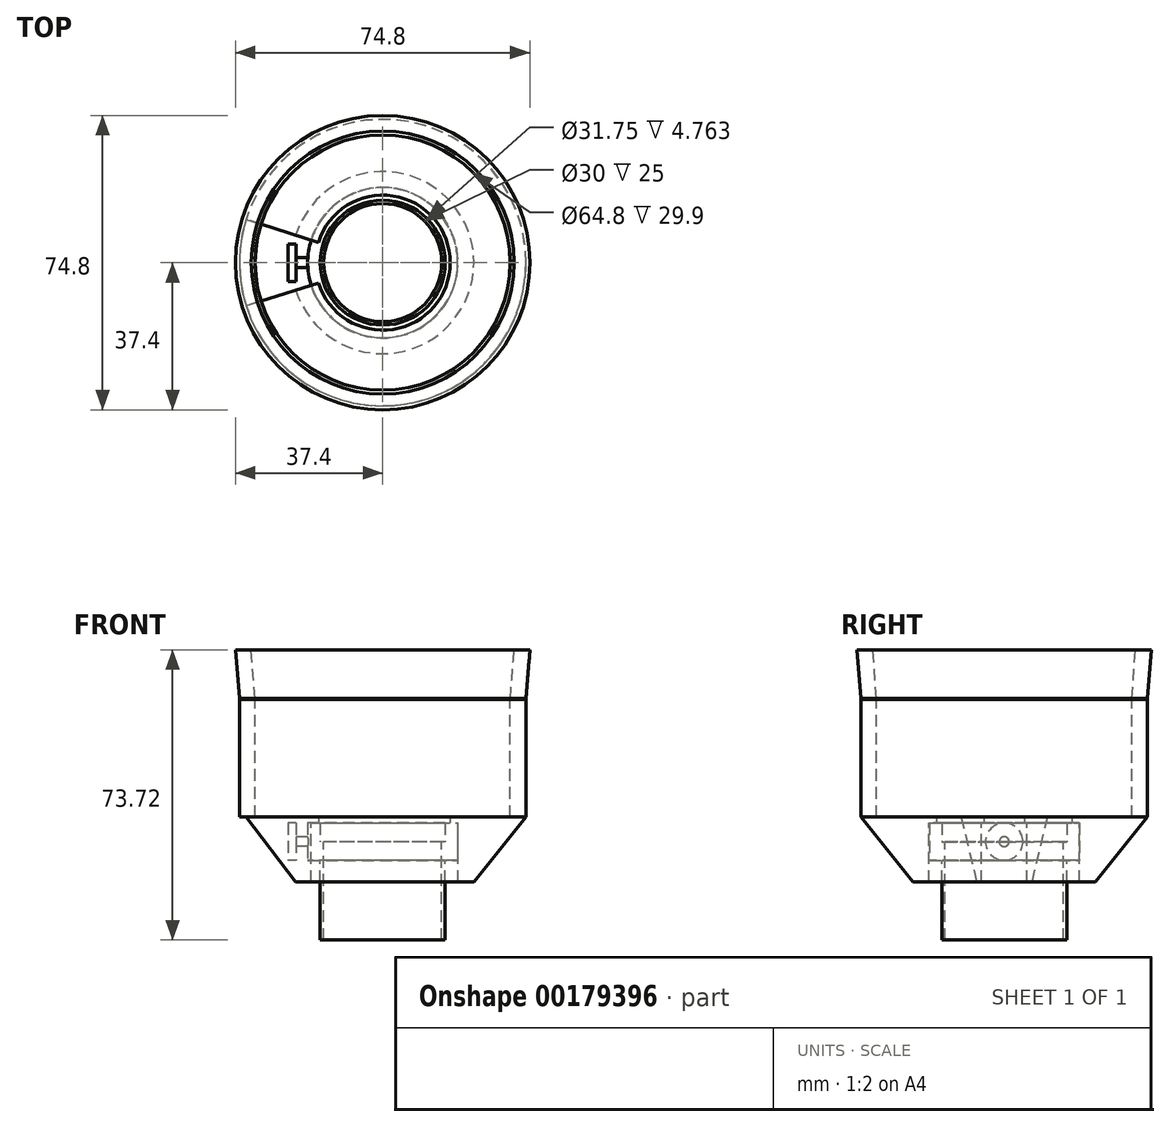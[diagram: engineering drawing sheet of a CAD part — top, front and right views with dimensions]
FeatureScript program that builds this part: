
annotation { "Feature Type Name" : "Feature", "Feature Type Description" : "" }
export const myFeature = defineFeature(function(context is Context, id is Id, definition is map)
    precondition{}
    {
        {
            var Q0;
            Q0=qCreatedBy(makeId("Top.planeOp"),FACE);
            var sketch = newSketch(context, id + "F0", { "sketchPlane" : qUnion([Q0])});
            skCircle(sketch, "E0", {"center": v(0, 0) * mm, "radius": 15.88 * mm});
            skCircle(sketch, "E1", {"center": v(0, 0) * mm, "radius": 19.05 * mm});
            skCircle(sketch, "E2", {"center": v(0, 0) * mm, "radius": 15 * mm});
            skLineSegment(sketch, "E3.bottom", {"start": v(-22.05, 1.24) * mm, "end": v(-19, 1.24) * mm});
            skLineSegment(sketch, "E3.top", {"start": v(-22.05, -1.26) * mm, "end": v(-19, -1.26) * mm});
            skPoint(sketch, "E3.middle", {"position": v(-19.05, 0) * mm});
            skLineSegment(sketch, "E4.bottom", {"start": v(-24.05, 4.76) * mm, "end": v(-22.05, 4.76) * mm});
            skLineSegment(sketch, "E4.top", {"start": v(-24.05, -4.77) * mm, "end": v(-22.05, -4.77) * mm});
            skLineSegment(sketch, "E4.left", {"start": v(-24.05, 4.76) * mm, "end": v(-24.05, -4.77) * mm});
            skLineSegment(sketch, "E4.right", {"start": v(-22.05, 4.76) * mm, "end": v(-22.05, 1.24) * mm});
            skLineSegment(sketch, "E5.trimOffspring", {"start": v(-22.05, -1.26) * mm, "end": v(-22.05, -4.77) * mm});
            skLineSegment(sketch, "E6", {"start": v(-24.05, 0) * mm, "end": v(-19.05, 0) * mm});
            skSolve(sketch);
        }
        {
            var Q0;
            Q0=makeQuery(id+"F0.imprint","IMPRINT",FACE,{"disambiguationData":[TD([[makeQuery(id+"F0.imprint","IMPRINT",EDGE,{"derivedFrom":sQuery(id+"F0.wireOp",EDGE,"E0")}),-1.0]])]});
            extrude(context, id + "F1", {"entities" : qUnion([Q0]), "endBound" : BoundingType.SYMMETRIC, "depth" : 9.53 * mm});
        }
        {
            var Q0;
            {var subQ3=sQuery(id+"F0.wireOp",EDGE,"E3.bottom");Q0=makeQuery(id+"F0.imprint","IMPRINT",FACE,{"disambiguationData":[TD([[makeQuery(id+"F0.imprint","IMPRINT",EDGE,{"derivedFrom":subQ3}),-1.0]])]});}
            var Q1;
            Q1=sQuery(id+"F0.wireOp",EDGE,"E6");
            revolve(context, id + "F2", {"operationType" : NewBodyOperationType.ADD, "entities" : qUnion([Q0]), "axis" : qUnion([Q1]), "revolveType" : RevolveType.FULL});
        }
        {
            var Q0;
            Q0=makeQuery(id+"F0.imprint","IMPRINT",FACE,{"disambiguationData":[TD([[makeQuery(id+"F0.imprint","IMPRINT",EDGE,{"derivedFrom":sQuery(id+"F0.wireOp",EDGE,"E0")}),1.0]])]});
            extrude(context, id + "F3", {"entities" : qUnion([Q0]), "operationType" : NewBodyOperationType.ADD, "oppositeDirection" : true, "depth" : 25 * mm});
        }
        {
            var Q0;
            Q0=makeQuery(id+"F1.opExtrude","CAP_FACE",FACE,{"disambiguationData":[OSD([sQuery(id+"F0.wireOp",EDGE,"E0"),sQuery(id+"F0.wireOp",EDGE,"E1")])],"isStart":false});
            var sketch = newSketch(context, id + "F4", { "sketchPlane" : qUnion([Q0])});
            skCircle(sketch, "E7.0", {"center": v(0, 0) * mm, "radius": 19.05 * mm});
            skLineSegment(sketch, "E8.0", {"start": v(-24.05, -4.76) * mm, "end": v(-24.05, 4.76) * mm});
            skLineSegment(sketch, "E9.0", {"start": v(-22.05, -4.76) * mm, "end": v(-22.05, 4.76) * mm});
            skCircle(sketch, "E10", {"center": v(0, 0) * mm, "radius": 19.15 * mm});
            skCircle(sketch, "E11", {"center": v(0, 0) * mm, "radius": 23.15 * mm});
            skLineSegment(sketch, "E12", {"start": v(0, 0) * mm, "end": v(-22.08, 6.96) * mm});
            skLineSegment(sketch, "E13", {"start": v(0, 0) * mm, "end": v(-22.08, -6.96) * mm});
            skLineSegment(sketch, "E14", {"start": v(-9.35, 0) * mm, "end": v(-9.35, -2.95) * mm});
            skLineSegment(sketch, "E15", {"start": v(-9.35, 0) * mm, "end": v(-9.35, 2.95) * mm});
            skCircle(sketch, "E16", {"center": v(0, 0) * mm, "radius": 17.15 * mm});
            skSolve(sketch);
        }
        {
            var Q0;
            {var subQ0=sQuery(id+"F4.wireOp",EDGE,"E12");var subQ1=sQuery(id+"F4.wireOp",EDGE,"E10");var subQ2=makeQuery(id+"F4.imprint","INTERSECT",VERTEX,{"derivedFrom":[subQ1,subQ0]});Q0=makeQuery(id+"F4.imprint","IMPRINT",FACE,{"disambiguationData":[TD([[makeQuery(id+"F4.imprint","IMPRINT",EDGE,{"disambiguationData":[TD([[subQ2,1.0]])],"derivedFrom":subQ1}),-1.0]])]});}
            extrude(context, id + "F5", {"entities" : qUnion([Q0]), "oppositeDirection" : true, "depth" : 15 * mm});
        }
        {
            var Q0;
            {var subQ0=sQuery(id+"F4.wireOp",EDGE,"E12");var subQ1=sQuery(id+"F4.wireOp",EDGE,"E7.0");var subQ2=makeQuery(id+"F4.imprint","INTERSECT",VERTEX,{"derivedFrom":[subQ1,subQ0]});Q0=makeQuery(id+"F4.imprint","IMPRINT",FACE,{"disambiguationData":[TD([[makeQuery(id+"F4.imprint","IMPRINT",EDGE,{"disambiguationData":[TD([[subQ2,1.0]])],"derivedFrom":subQ1}),1.0]])]});}
            var Q1;
            {var subQ0=sQuery(id+"F4.wireOp",EDGE,"E12");var subQ1=sQuery(id+"F4.wireOp",EDGE,"E10");var subQ2=makeQuery(id+"F4.imprint","INTERSECT",VERTEX,{"derivedFrom":[subQ1,subQ0]});Q1=makeQuery(id+"F4.imprint","IMPRINT",FACE,{"disambiguationData":[TD([[makeQuery(id+"F4.imprint","IMPRINT",EDGE,{"disambiguationData":[TD([[subQ2,1.0]])],"derivedFrom":subQ1}),-1.0]])]});}
            var Q2;
            {var subQ0=sQuery(id+"F4.wireOp",EDGE,"E12");var subQ1=sQuery(id+"F4.wireOp",EDGE,"E7.0");var subQ2=makeQuery(id+"F4.imprint","INTERSECT",VERTEX,{"derivedFrom":[subQ1,subQ0]});Q2=makeQuery(id+"F4.imprint","IMPRINT",FACE,{"disambiguationData":[TD([[makeQuery(id+"F4.imprint","IMPRINT",EDGE,{"disambiguationData":[TD([[subQ2,1.0]])],"derivedFrom":subQ1}),-1.0]])]});}
            extrude(context, id + "F6", {"entities" : qUnion([Q0, Q1, Q2]), "operationType" : NewBodyOperationType.ADD, "depth" : 1.5 * mm});
        }
        {
            var Q0;
            Q0=makeQuery(id+"F6.opExtrude","CAP_FACE",FACE,{"disambiguationData":[OSD([sQuery(id+"F4.wireOp",EDGE,"E11"),sQuery(id+"F4.wireOp",EDGE,"E12"),sQuery(id+"F4.wireOp",EDGE,"E13"),sQuery(id+"F4.wireOp",EDGE,"E16")])],"isStart":false});
            var sketch = newSketch(context, id + "F7", { "sketchPlane" : qUnion([Q0])});
            skCircle(sketch, "E17.0", {"center": v(0, 0) * mm, "radius": 23.15 * mm});
            skCircle(sketch, "E18", {"center": v(0, 0) * mm, "radius": 32.4 * mm});
            skCircle(sketch, "E19", {"center": v(0, 0) * mm, "radius": 36.4 * mm});
            skLineSegment(sketch, "E20.0", {"start": v(-16.36, 5.16) * mm, "end": v(-22.08, 6.96) * mm});
            skLineSegment(sketch, "E21.0", {"start": v(-16.36, -5.16) * mm, "end": v(-22.08, -6.96) * mm});
            skLineSegment(sketch, "E22", {"start": v(-22.08, 6.96) * mm, "end": v(-34.72, 10.95) * mm});
            skLineSegment(sketch, "E23", {"start": v(-22.08, -6.96) * mm, "end": v(-34.72, -10.95) * mm});
            skLineSegment(sketch, "E24", {"start": v(-22.08, -6.96) * mm, "end": v(-35.73, -6.96) * mm});
            skLineSegment(sketch, "E25", {"start": v(-22.08, 6.96) * mm, "end": v(-35.73, 6.96) * mm});
            skSolve(sketch);
        }
        {
            var Q0;
            Q0=qCreatedBy(makeId("Right.planeOp"),FACE);
            var sketch = newSketch(context, id + "F8", { "sketchPlane" : qUnion([Q0])});
            skLineSegment(sketch, "E26.0", {"start": v(-36.4, 6.26) * mm, "end": v(36.4, 6.26) * mm});
            skLineSegment(sketch, "E27.0", {"start": v(-23.15, -10.24) * mm, "end": v(23.15, -10.24) * mm});
            skLineSegment(sketch, "E28.0.0", {"start": v(6.96, -10.24) * mm, "end": v(6.96, 6.26) * mm});
            skLineSegment(sketch, "E28.0.1", {"start": v(23.15, 6.26) * mm, "end": v(-23.15, 6.26) * mm});
            skLineSegment(sketch, "E28.0.2", {"start": v(-6.96, 6.26) * mm, "end": v(-6.96, -10.24) * mm});
            skLineSegment(sketch, "E29", {"start": v(36.4, 6.26) * mm, "end": v(23.15, -10.24) * mm});
            skLineSegment(sketch, "E30", {"start": v(23.15, 6.26) * mm, "end": v(23.15, -10.24) * mm});
            skLineSegment(sketch, "E31", {"start": v(0, 6.26) * mm, "end": v(0, -27.02) * mm});
            skPoint(sketch, "E31.endSnap0", {"position": v(0, 6.26) * mm});
            skSolve(sketch);
        }
        {
            var Q0;
            {var subQ0=sQuery(id+"F8.wireOp",EDGE,"E29");Q0=makeQuery(id+"F8.imprint","IMPRINT",FACE,{"disambiguationData":[TD([[makeQuery(id+"F8.imprint","IMPRINT",EDGE,{"derivedFrom":subQ0}),-1.0]])]});}
            var Q1;
            Q1=sQuery(id+"F8.wireOp",EDGE,"E31");
            revolve(context, id + "F9", {"operationType" : NewBodyOperationType.ADD, "entities" : qUnion([Q0]), "axis" : qUnion([Q1]), "revolveType" : RevolveType.TWO_DIRECTIONS, "angle" : 252.5 * degree, "angleBack" : 287.5 * degree});
        }
        {
            var Q0;
            Q0=qCreatedBy(makeId("Right.planeOp"),FACE);
            var sketch = newSketch(context, id + "F10", { "sketchPlane" : qUnion([Q0])});
            skLineSegment(sketch, "E32.0", {"start": v(-36.4, 6.26) * mm, "end": v(36.4, 6.26) * mm});
            skLineSegment(sketch, "E33.0", {"start": v(-32.4, 6.26) * mm, "end": v(32.4, 6.26) * mm});
            skLineSegment(sketch, "E34", {"start": v(36.4, 36.26) * mm, "end": v(36.4, 6.26) * mm});
            skLineSegment(sketch, "E35", {"start": v(32.4, 36.26) * mm, "end": v(32.4, 6.26) * mm});
            skLineSegment(sketch, "E36.MirrorCS", {"start": v(-36.4, 36.26) * mm, "end": v(-36.4, 6.26) * mm});
            skLineSegment(sketch, "E37.MirrorCS", {"start": v(-32.4, 36.26) * mm, "end": v(-32.4, 6.26) * mm});
            skLineSegment(sketch, "E38", {"start": v(32.4, 36.26) * mm, "end": v(33.4, 48.72) * mm});
            skLineSegment(sketch, "E39", {"start": v(33.4, 48.72) * mm, "end": v(37.4, 48.72) * mm});
            skLineSegment(sketch, "E40", {"start": v(37.4, 48.72) * mm, "end": v(36.4, 36.26) * mm});
            skLineSegment(sketch, "E41.MirrorCS", {"start": v(-32.4, 36.26) * mm, "end": v(-33.4, 48.72) * mm});
            skLineSegment(sketch, "E42.MirrorCS", {"start": v(-33.4, 48.72) * mm, "end": v(-37.4, 48.72) * mm});
            skLineSegment(sketch, "E43.MirrorCS", {"start": v(-37.4, 48.72) * mm, "end": v(-36.4, 36.26) * mm});
            skSolve(sketch);
        }
        {
            var Q0;
            {var subQ1=sQuery(id+"F10.wireOp",EDGE,"E34");Q0=makeQuery(id+"F10.imprint","IMPRINT",FACE,{"disambiguationData":[TD([[makeQuery(id+"F10.imprint","IMPRINT",EDGE,{"derivedFrom":subQ1}),-1.0]])]});}
            var Q1;
            Q1=sQuery(id+"F8.wireOp",EDGE,"E31");
            revolve(context, id + "F11", {"operationType" : NewBodyOperationType.ADD, "entities" : qUnion([Q0]), "axis" : qUnion([Q1]), "revolveType" : RevolveType.FULL});
        }
        {
            var Q0;
            Q0=makeQuery(id+"F11.opRevolve","SWEPT_EDGE",EDGE,{"disambiguationData":[OSD([sQuery(id+"F10.wireOp",EDGE,"E35"),sQuery(id+"F10.wireOp",EDGE,"E38")])]});
            chamfer(context, id + "F12", {"entities" : qUnion([Q0]), "width" : 2.5 * mm, "tangentPropagation" : true});
        }
        {
            var Q0;
            Q0=makeQuery(id+"F11.opRevolve","SWEPT_EDGE",EDGE,{"disambiguationData":[OSD([sQuery(id+"F10.wireOp",EDGE,"E34"),sQuery(id+"F10.wireOp",EDGE,"E40")])]});
            chamfer(context, id + "F13", {"entities" : qUnion([Q0]), "width" : 2.5 * mm, "tangentPropagation" : true});
        }
        {
            var Q0;
            {var subQ0=sQuery(id+"F10.wireOp",EDGE,"E40");Q0=makeQuery(id+"F13.opChamfer","BLEND_EDGE",EDGE,{"blendedFrom":[makeQuery(id+"F11.opRevolve","SWEPT_EDGE",EDGE,{"disambiguationData":[OSD([sQuery(id+"F10.wireOp",EDGE,"E34"),subQ0])]}),makeQuery(id+"F11.opRevolve","SWEPT_FACE",FACE,{"disambiguationData":[OSD([subQ0])]})],"blendedInto":[makeQuery(id+"F11.opRevolve","SWEPT_FACE",FACE,{"disambiguationData":[OSD([subQ0])]})]});}
            var Q1;
            {var subQ0=sQuery(id+"F10.wireOp",EDGE,"E34");Q1=makeQuery(id+"F13.opChamfer","BLEND_EDGE",EDGE,{"blendedFrom":[makeQuery(id+"F11.opRevolve","SWEPT_EDGE",EDGE,{"disambiguationData":[OSD([subQ0,sQuery(id+"F10.wireOp",EDGE,"E40")])]}),makeQuery(id+"F11.opRevolve","SWEPT_FACE",FACE,{"disambiguationData":[OSD([subQ0])]})],"blendedInto":[makeQuery(id+"F11.opRevolve","SWEPT_FACE",FACE,{"disambiguationData":[OSD([subQ0])]})]});}
            chamfer(context, id + "F14", {"entities" : qUnion([Q0, Q1]), "width" : 2.5 * mm, "tangentPropagation" : true});
        }
    });
